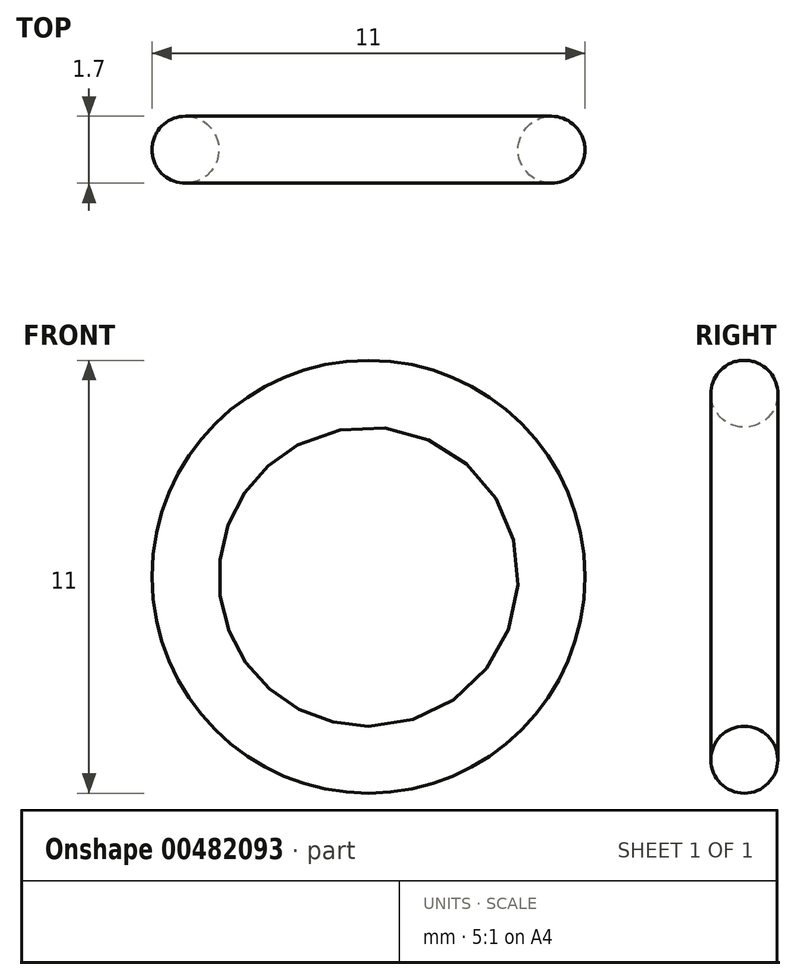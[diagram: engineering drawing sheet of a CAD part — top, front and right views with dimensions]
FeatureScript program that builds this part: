
annotation { "Feature Type Name" : "Feature", "Feature Type Description" : "" }
export const myFeature = defineFeature(function(context is Context, id is Id, definition is map)
    precondition{}
    {
        {
            var Q0;
            Q0=qCreatedBy(makeId("Front.planeOp"),FACE);
            var sketch = newSketch(context, id + "F0", { "sketchPlane" : qUnion([Q0])});
            skCircle(sketch, "E0", {"center": v(0, 0) * mm, "radius": 5.5 * mm});
            skSolve(sketch);
        }
        {
            var Q0;
            Q0=qCreatedBy(makeId("Top.planeOp"),FACE);
            var sketch = newSketch(context, id + "F1", { "sketchPlane" : qUnion([Q0])});
            skCircle(sketch, "E1", {"center": v(4.65, 0) * mm, "radius": 0.85 * mm});
            skLineSegment(sketch, "E2.0", {"start": v(5.5, 0) * mm, "end": v(-5.5, 0) * mm});
            skSolve(sketch);
        }
        {
            var Q0;
            {var subQ0=sQuery(id+"F1.wireOp",EDGE,"E2.0");var subQ1=sQuery(id+"F1.wireOp",EDGE,"E1");var subQ2=makeQuery(id+"F1.imprint","INTERSECT",VERTEX,{"disambiguationData":[OD(0.0)],"derivedFrom":[subQ1,subQ0]});Q0=makeQuery(id+"F1.imprint","IMPRINT",FACE,{"disambiguationData":[TD([[makeQuery(id+"F1.imprint","IMPRINT",EDGE,{"disambiguationData":[TD([[subQ2,1.0]])],"derivedFrom":subQ1}),1.0]])]});}
            var Q1;
            {var subQ0=sQuery(id+"F1.wireOp",EDGE,"E2.0");var subQ1=sQuery(id+"F1.wireOp",EDGE,"E1");var subQ2=makeQuery(id+"F1.imprint","INTERSECT",VERTEX,{"disambiguationData":[OD(0.0)],"derivedFrom":[subQ1,subQ0]});Q1=makeQuery(id+"F1.imprint","IMPRINT",FACE,{"disambiguationData":[TD([[makeQuery(id+"F1.imprint","IMPRINT",EDGE,{"disambiguationData":[TD([[subQ2,-1.0]])],"derivedFrom":subQ1}),1.0]])]});}
            var Q2;
            Q2=sQuery(id+"F0.wireOp",EDGE,"E0");
            sweep(context, id + "F2", {"profiles" : qUnion([Q0, Q1]), "path" : qUnion([Q2])});
        }
    });
